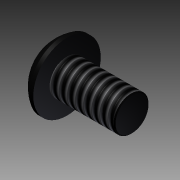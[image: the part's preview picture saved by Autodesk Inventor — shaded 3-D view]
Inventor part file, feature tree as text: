
AUTODESK INVENTOR PART (.ipt)
format: ipt  version: 2011 (Build 150239000, 239)  size: 117,760 bytes
history: native  units: in
note: dims shown in document units (in); Inventor stores cm internally (conversion verified against a paired STEP export)
features: other x1, imported_body x1, thread x1
ambient origin geometry x8: Origin, YZ Plane, XZ Plane, XY Plane, X Axis, Y Axis, Z Axis, Center Point
feature tree (3):
  parser-record x1  (decoder bookkeeping rows leaked as tree rows — omitted from the tree; the rows remain in map.json)
  imported_body  "Base1"
  thread  "Thread1"  [1 undecoded]
note: 1 required parameter value undecoded (feature->parameter linkage not recoverable at this tier; creation-order binding heuristic only, values carry confidence <= 0.55)
